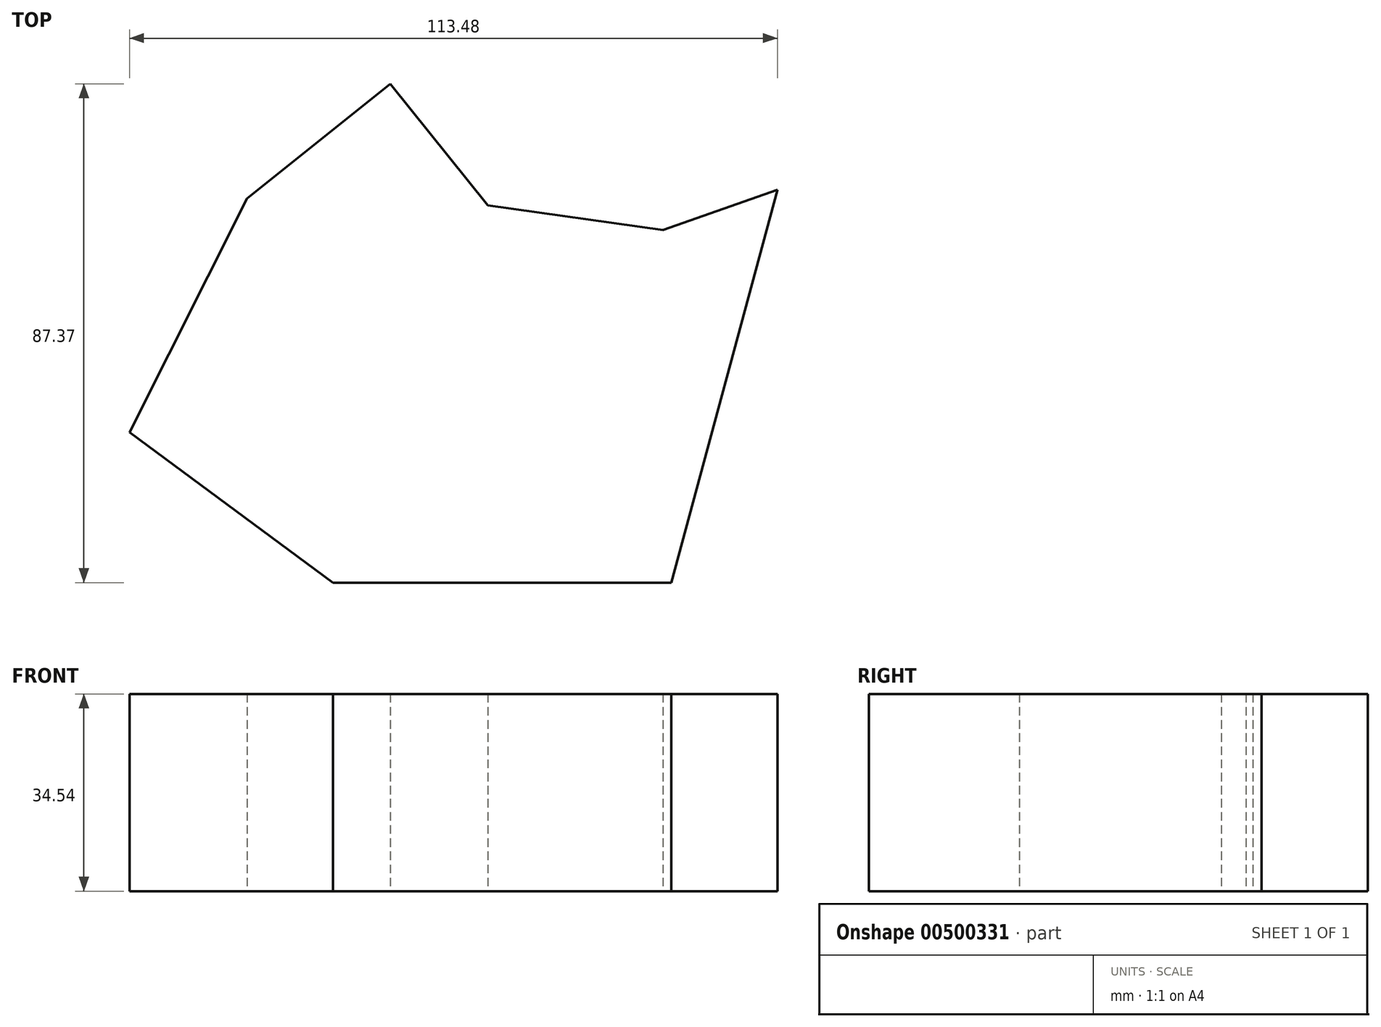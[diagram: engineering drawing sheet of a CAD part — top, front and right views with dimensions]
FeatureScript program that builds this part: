
annotation { "Feature Type Name" : "Feature", "Feature Type Description" : "" }
export const myFeature = defineFeature(function(context is Context, id is Id, definition is map)
    precondition{}
    {
        {
            var Q0;
            Q0=qCreatedBy(makeId("Top.planeOp"),FACE);
            var sketch = newSketch(context, id + "F0", { "sketchPlane" : qUnion([Q0])});
            skLineSegment(sketch, "E0", {"start": v(-49.02, 40.95) * mm, "end": v(-23.9, 61.03) * mm});
            skLineSegment(sketch, "E1", {"start": v(-23.9, 61.03) * mm, "end": v(-6.86, 39.72) * mm});
            skLineSegment(sketch, "E2", {"start": v(-6.86, 39.72) * mm, "end": v(23.8, 35.43) * mm});
            skLineSegment(sketch, "E3", {"start": v(23.8, 35.43) * mm, "end": v(43.88, 42.46) * mm});
            skLineSegment(sketch, "E4", {"start": v(43.88, 42.46) * mm, "end": v(25.3, -26.34) * mm});
            skLineSegment(sketch, "E5", {"start": v(25.3, -26.34) * mm, "end": v(-33.95, -26.34) * mm});
            skLineSegment(sketch, "E6", {"start": v(-33.95, -26.34) * mm, "end": v(-69.6, 0) * mm});
            skLineSegment(sketch, "E7", {"start": v(-69.6, 0) * mm, "end": v(-49.02, 40.95) * mm});
            skSolve(sketch);
        }
        {
            var Q0;
            Q0=makeQuery(id+"F0.imprint","IMPRINT",FACE,{"disambiguationData":[TD([[makeQuery(id+"F0.imprint","IMPRINT",EDGE,{"derivedFrom":sQuery(id+"F0.wireOp",EDGE,"E0")}),-1.0]])]});
            extrude(context, id + "F1", {"entities" : qUnion([Q0]), "depth" : 34.54 * mm});
        }
    });
